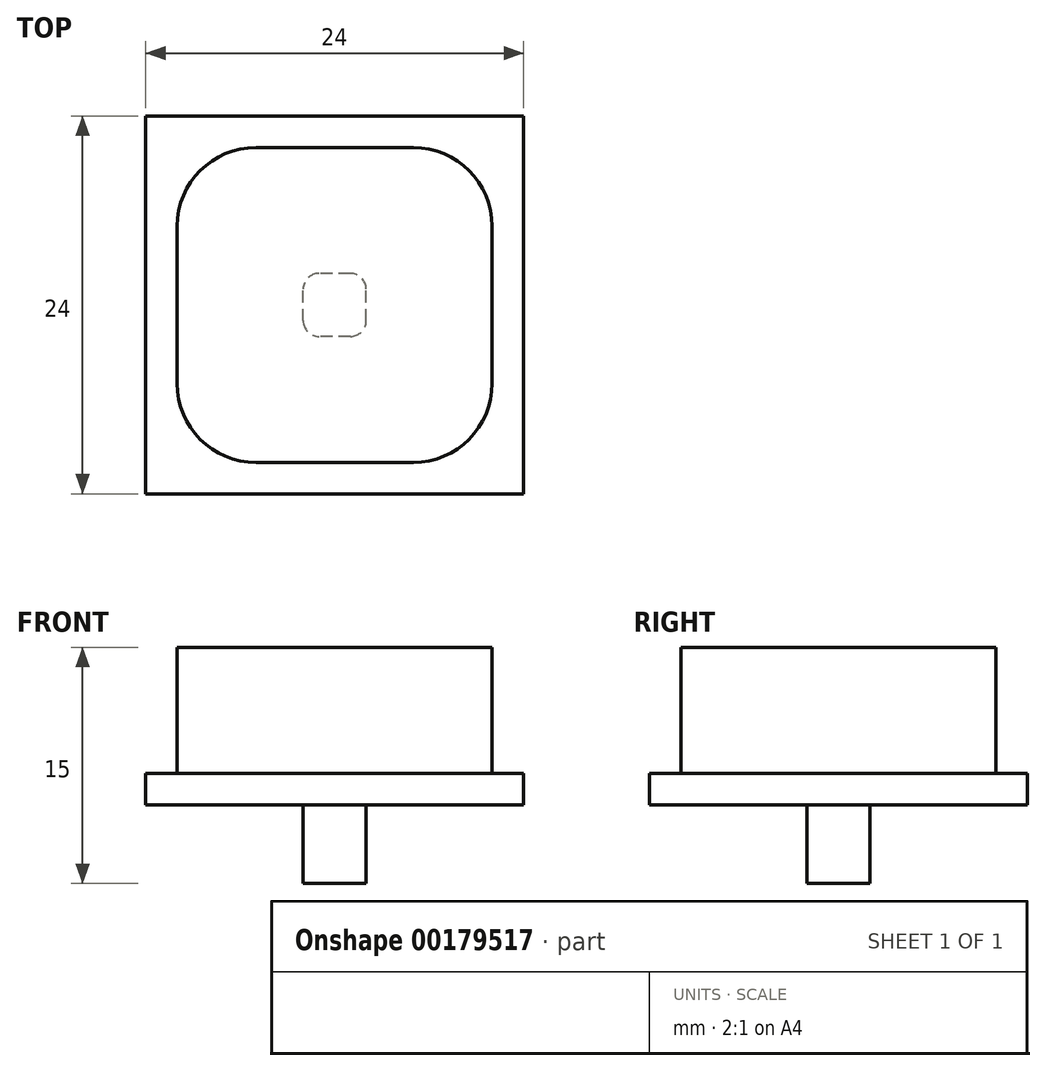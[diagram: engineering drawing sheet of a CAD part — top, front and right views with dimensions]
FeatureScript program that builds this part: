
annotation { "Feature Type Name" : "Feature", "Feature Type Description" : "" }
export const myFeature = defineFeature(function(context is Context, id is Id, definition is map)
    precondition{}
    {
        {
            var Q0;
            Q0=qCreatedBy(makeId("Top.planeOp"),FACE);
            var sketch = newSketch(context, id + "F0", { "sketchPlane" : qUnion([Q0])});
            skPoint(sketch, "E0.middle", {"position": v(0, 0) * mm});
            skLineSegment(sketch, "E1.bottom", {"start": v(2, -2) * mm, "end": v(-2, -2) * mm});
            skLineSegment(sketch, "E1.top", {"start": v(2, 2) * mm, "end": v(-2, 2) * mm});
            skLineSegment(sketch, "E1.left", {"start": v(2, -2) * mm, "end": v(2, 2) * mm});
            skLineSegment(sketch, "E1.right", {"start": v(-2, -2) * mm, "end": v(-2, 2) * mm});
            skCircle(sketch, "E2", {"center": v(0, 0) * mm, "radius": 1.6 * mm});
            skLineSegment(sketch, "E3.bottom", {"start": v(10, -10) * mm, "end": v(-10, -10) * mm});
            skLineSegment(sketch, "E3.top", {"start": v(10, 10) * mm, "end": v(-10, 10) * mm});
            skLineSegment(sketch, "E3.left", {"start": v(10, -10) * mm, "end": v(10, 10) * mm});
            skLineSegment(sketch, "E3.right", {"start": v(-10, -10) * mm, "end": v(-10, 10) * mm});
            skLineSegment(sketch, "E4.bottom", {"start": v(12, -12) * mm, "end": v(-12, -12) * mm});
            skLineSegment(sketch, "E4.top", {"start": v(12, 12) * mm, "end": v(-12, 12) * mm});
            skLineSegment(sketch, "E4.left", {"start": v(12, -12) * mm, "end": v(12, 12) * mm});
            skLineSegment(sketch, "E4.right", {"start": v(-12, -12) * mm, "end": v(-12, 12) * mm});
            skSolve(sketch);
        }
        {
            var Q0;
            Q0=makeQuery(id+"F0.imprint","IMPRINT",FACE,{"disambiguationData":[TD([[makeQuery(id+"F0.imprint","IMPRINT",EDGE,{"derivedFrom":sQuery(id+"F0.wireOp",EDGE,"E1.bottom")}),1.0]])]});
            var Q1;
            Q1=makeQuery(id+"F0.imprint","IMPRINT",FACE,{"disambiguationData":[TD([[makeQuery(id+"F0.imprint","IMPRINT",EDGE,{"derivedFrom":sQuery(id+"F0.wireOp",EDGE,"E2")}),1.0]])]});
            var Q2;
            Q2=makeQuery(id+"F0.imprint","IMPRINT",FACE,{"disambiguationData":[TD([[makeQuery(id+"F0.imprint","IMPRINT",EDGE,{"derivedFrom":sQuery(id+"F0.wireOp",EDGE,"E1.bottom")}),-1.0]])]});
            extrude(context, id + "F1", {"entities" : qUnion([Q0, Q1, Q2]), "depth" : 10 * mm});
        }
        {
            var Q0;
            Q0=makeQuery(id+"F0.imprint","IMPRINT",FACE,{"disambiguationData":[TD([[makeQuery(id+"F0.imprint","IMPRINT",EDGE,{"derivedFrom":sQuery(id+"F0.wireOp",EDGE,"E3.bottom")}),1.0]])]});
            extrude(context, id + "F2", {"entities" : qUnion([Q0]), "operationType" : NewBodyOperationType.ADD, "depth" : 2 * mm});
        }
        {
            var Q0;
            Q0=makeQuery(id+"F0.imprint","IMPRINT",FACE,{"disambiguationData":[TD([[makeQuery(id+"F0.imprint","IMPRINT",EDGE,{"derivedFrom":sQuery(id+"F0.wireOp",EDGE,"E1.bottom")}),-1.0]])]});
            var Q1;
            Q1=makeQuery(id+"F0.imprint","IMPRINT",FACE,{"disambiguationData":[TD([[makeQuery(id+"F0.imprint","IMPRINT",EDGE,{"derivedFrom":sQuery(id+"F0.wireOp",EDGE,"E2")}),1.0]])]});
            extrude(context, id + "F3", {"entities" : qUnion([Q0, Q1]), "operationType" : NewBodyOperationType.ADD, "oppositeDirection" : true, "depth" : 5 * mm});
        }
        {
            var Q0;
            Q0=sQuery(id+"F0.wireOp",EDGE,"E2");
            extrude(context, id + "F4", {"bodyType" : ToolBodyType.SURFACE, "surfaceEntities" : qUnion([Q0]), "endBound" : BoundingType.SYMMETRIC, "oppositeDirection" : true, "depth" : 7 * mm});
        }
        {
            var Q0;
            Q0=makeQuery(id+"F1.opExtrude","SWEPT_EDGE",EDGE,{"disambiguationData":[OSD([sQuery(id+"F0.wireOp",EDGE,"E3.bottom"),sQuery(id+"F0.wireOp",EDGE,"E3.right")])]});
            fillet(context, id + "F5", {"entities" : qUnion([Q0]), "radius" : 5 * mm, "tangentPropagation" : true, "allowEdgeOverflow" : false});
        }
        {
            var Q0;
            Q0=makeQuery(id+"F1.opExtrude","SWEPT_EDGE",EDGE,{"disambiguationData":[OSD([sQuery(id+"F0.wireOp",EDGE,"E3.bottom"),sQuery(id+"F0.wireOp",EDGE,"E3.left")])]});
            var Q1;
            Q1=makeQuery(id+"F1.opExtrude","SWEPT_EDGE",EDGE,{"disambiguationData":[OSD([sQuery(id+"F0.wireOp",EDGE,"E3.top"),sQuery(id+"F0.wireOp",EDGE,"E3.left")])]});
            var Q2;
            Q2=makeQuery(id+"F1.opExtrude","SWEPT_EDGE",EDGE,{"disambiguationData":[OSD([sQuery(id+"F0.wireOp",EDGE,"E3.top"),sQuery(id+"F0.wireOp",EDGE,"E3.right")])]});
            fillet(context, id + "F6", {"entities" : qUnion([Q0, Q1, Q2]), "radius" : 5 * mm, "tangentPropagation" : true, "allowEdgeOverflow" : false});
        }
        {
            var Q0;
            Q0=makeQuery(id+"F3.opExtrude","SWEPT_EDGE",EDGE,{"disambiguationData":[OSD([sQuery(id+"F0.wireOp",EDGE,"E1.top"),sQuery(id+"F0.wireOp",EDGE,"E1.left")])]});
            var Q1;
            Q1=makeQuery(id+"F3.opExtrude","SWEPT_EDGE",EDGE,{"disambiguationData":[OSD([sQuery(id+"F0.wireOp",EDGE,"E1.bottom"),sQuery(id+"F0.wireOp",EDGE,"E1.left")])]});
            var Q2;
            Q2=makeQuery(id+"F3.opExtrude","SWEPT_EDGE",EDGE,{"disambiguationData":[OSD([sQuery(id+"F0.wireOp",EDGE,"E1.bottom"),sQuery(id+"F0.wireOp",EDGE,"E1.right")])]});
            var Q3;
            Q3=makeQuery(id+"F3.opExtrude","SWEPT_EDGE",EDGE,{"disambiguationData":[OSD([sQuery(id+"F0.wireOp",EDGE,"E1.top"),sQuery(id+"F0.wireOp",EDGE,"E1.right")])]});
            fillet(context, id + "F7", {"entities" : qUnion([Q0, Q1, Q2, Q3]), "radius" : 1 * mm, "tangentPropagation" : true, "allowEdgeOverflow" : false});
        }
    });
